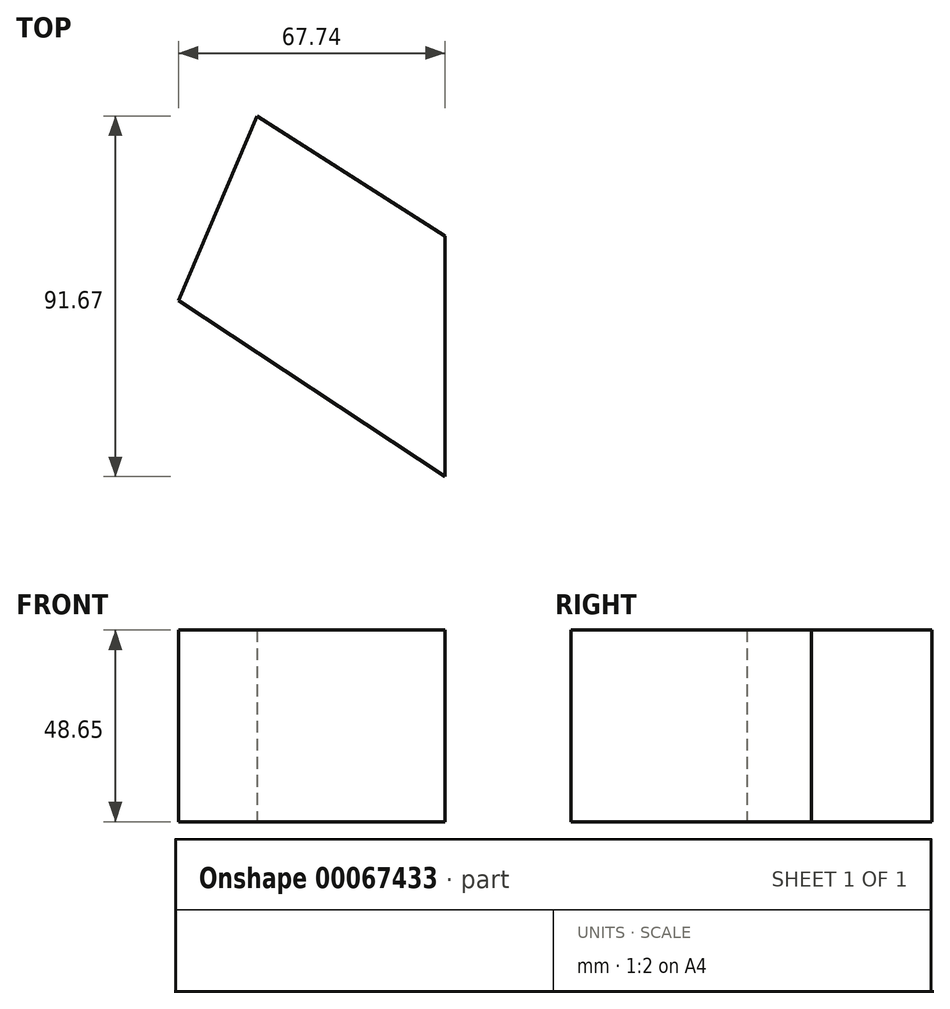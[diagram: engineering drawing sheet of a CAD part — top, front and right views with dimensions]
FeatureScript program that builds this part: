
annotation { "Feature Type Name" : "Feature", "Feature Type Description" : "" }
export const myFeature = defineFeature(function(context is Context, id is Id, definition is map)
    precondition{}
    {
        {
            var Q0;
            Q0=qCreatedBy(makeId("Top.planeOp"),FACE);
            var sketch = newSketch(context, id + "F0", { "sketchPlane" : qUnion([Q0])});
            skLineSegment(sketch, "E0", {"start": v(-109.71, 53.9) * mm, "end": v(-41.97, 9.17) * mm});
            skLineSegment(sketch, "E1", {"start": v(-41.97, 9.17) * mm, "end": v(-41.97, 70.25) * mm});
            skLineSegment(sketch, "E2", {"start": v(-41.97, 70.25) * mm, "end": v(-89.66, 100.84) * mm});
            skLineSegment(sketch, "E3", {"start": v(-89.66, 100.84) * mm, "end": v(-109.71, 53.9) * mm});
            skSolve(sketch);
        }
        {
            var Q0;
            Q0 = qSketchRegion(id + "F0", true);
            extrude(context, id + "F1", {"entities" : qUnion([Q0]), "depth" : 48.65 * mm});
        }
    });
